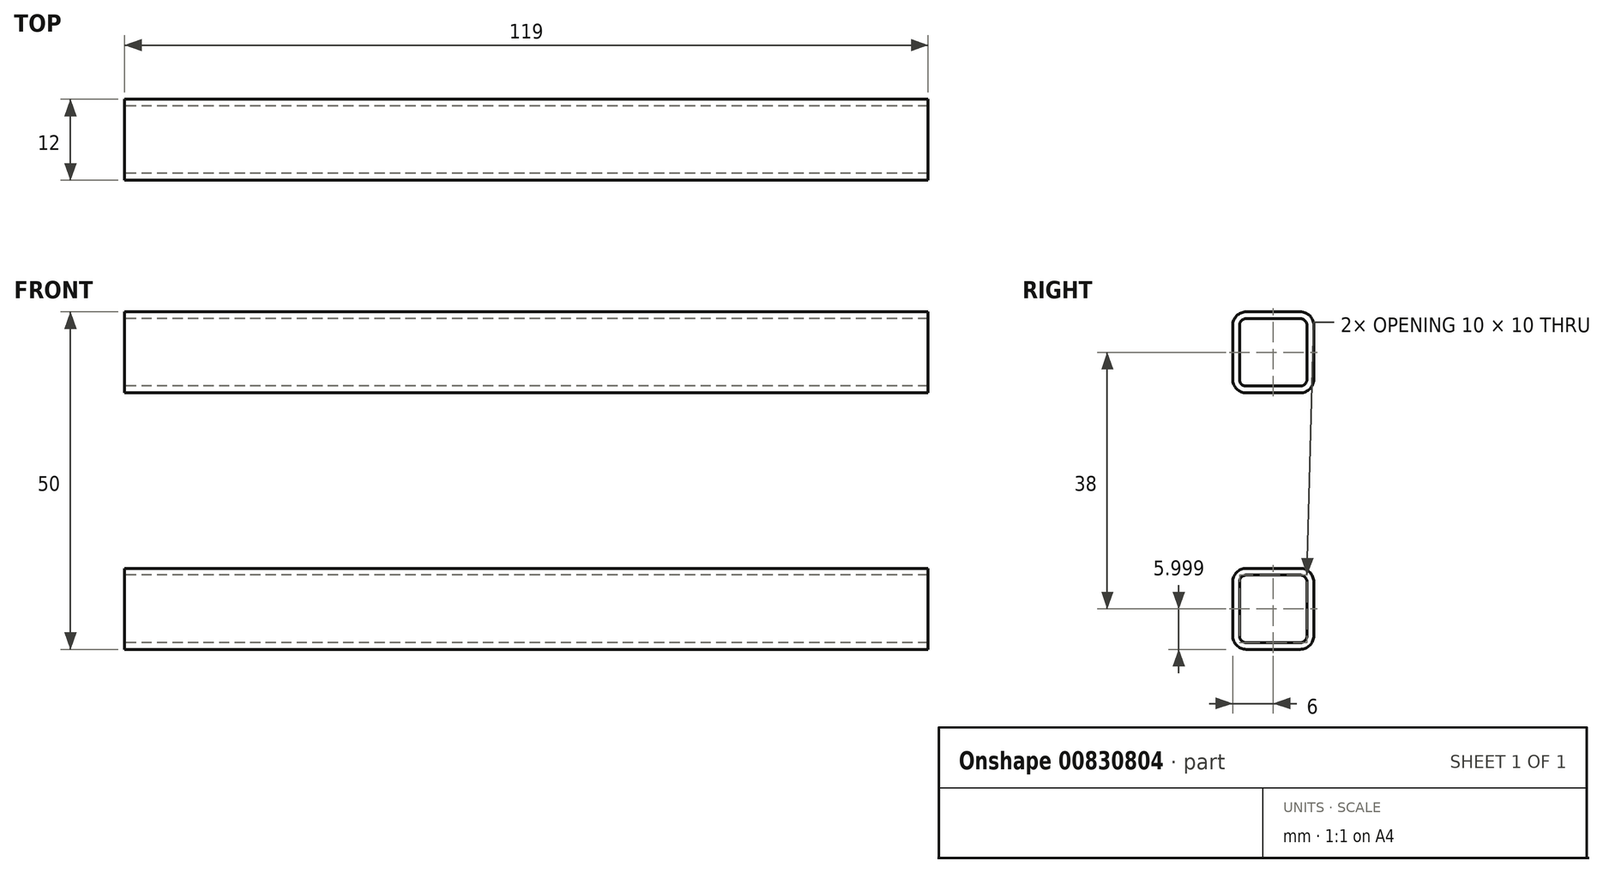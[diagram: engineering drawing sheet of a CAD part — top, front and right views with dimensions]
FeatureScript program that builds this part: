
annotation { "Feature Type Name" : "Feature", "Feature Type Description" : "" }
export const myFeature = defineFeature(function(context is Context, id is Id, definition is map)
    precondition{}
    {
        {
            var Q0;
            Q0=qCreatedBy(makeId("Front.planeOp"),FACE);
            var sketch = newSketch(context, id + "F0", { "sketchPlane" : qUnion([Q0])});
            skLineSegment(sketch, "E0", {"start": v(-60.2, 31.39) * mm, "end": v(58.8, 31.39) * mm});
            skLineSegment(sketch, "E1", {"start": v(-56.2, 36.39) * mm, "end": v(-56.2, -28.61) * mm});
            skLineSegment(sketch, "E2", {"start": v(53.8, 36.39) * mm, "end": v(53.8, -23.61) * mm});
            skLineSegment(sketch, "E3", {"start": v(58.8, -18.61) * mm, "end": v(-60.2, -18.61) * mm});
            skSolve(sketch);
        }
        {
            var Q0;
            Q0=sQuery(id+"F0.wireOp",VERTEX,"E1.end");
            var Q1;
            Q1=sQuery(id+"F0.wireOp",EDGE,"E1");
            cPlane(context, id + "F1", {"entities" : qUnion([Q0, Q1]), "cplaneType" : CPlaneType.LINE_POINT, "offset" : 150 * mm, "width" : 150 * mm, "height" : 150 * mm});
        }
        {
            var Q0;
            Q0=sQuery(id+"F0.wireOp",VERTEX,"E1.start");
            var Q1;
            Q1=sQuery(id+"F0.wireOp",EDGE,"E1");
            cPlane(context, id + "F2", {"entities" : qUnion([Q0, Q1]), "cplaneType" : CPlaneType.LINE_POINT, "offset" : 150 * mm, "width" : 150 * mm, "height" : 150 * mm});
        }
        {
            var Q0;
            Q0=qCreatedBy(id+"F1.planeOp",FACE);
            var sketch = newSketch(context, id + "F3", { "sketchPlane" : qUnion([Q0])});
            skLineSegment(sketch, "E4.bottom", {"start": v(-54.2, -12.5) * mm, "end": v(-46.2, -12.5) * mm});
            skLineSegment(sketch, "E4.top", {"start": v(-54.2, 12.5) * mm, "end": v(-46.2, 12.5) * mm});
            skLineSegment(sketch, "E4.left", {"start": v(-56.2, -10.5) * mm, "end": v(-56.2, 10.5) * mm});
            skLineSegment(sketch, "E4.right", {"start": v(-44.2, -10.5) * mm, "end": v(-44.2, 10.5) * mm});
            skPoint(sketch, "E5.visualSharp", {"position": v(-56.2, 12.5) * mm});
            skArc(sketch, "E5.filletArc", {"start": v(-54.2, 12.5) * mm, "mid": v(-55.62, 11.91) * mm, "end": v(-56.2, 10.5) * mm});
            skPoint(sketch, "E6.visualSharp", {"position": v(-44.2, 12.5) * mm});
            skArc(sketch, "E6.filletArc", {"start": v(-44.2, 10.5) * mm, "mid": v(-44.8, 11.91) * mm, "end": v(-46.2, 12.5) * mm});
            skPoint(sketch, "E7.visualSharp", {"position": v(-44.2, -12.5) * mm});
            skArc(sketch, "E7.filletArc", {"start": v(-46.2, -12.5) * mm, "mid": v(-44.8, -11.91) * mm, "end": v(-44.2, -10.5) * mm});
            skPoint(sketch, "E8.visualSharp", {"position": v(-56.2, -12.5) * mm});
            skArc(sketch, "E8.filletArc", {"start": v(-56.2, -10.5) * mm, "mid": v(-55.62, -11.91) * mm, "end": v(-54.2, -12.5) * mm});
            skArc(sketch, "E9.0", {"start": v(-54.2, 11.5) * mm, "mid": v(-54.91, 11.2) * mm, "end": v(-55.2, 10.5) * mm});
            skLineSegment(sketch, "E9.1", {"start": v(-55.2, -10.5) * mm, "end": v(-55.2, 10.5) * mm});
            skArc(sketch, "E9.2", {"start": v(-55.2, -10.5) * mm, "mid": v(-54.91, -11.2) * mm, "end": v(-54.2, -11.5) * mm});
            skLineSegment(sketch, "E9.3", {"start": v(-54.2, -11.5) * mm, "end": v(-46.2, -11.5) * mm});
            skArc(sketch, "E9.4", {"start": v(-46.2, -11.5) * mm, "mid": v(-45.5, -11.2) * mm, "end": v(-45.2, -10.5) * mm});
            skLineSegment(sketch, "E9.5", {"start": v(-54.2, 11.5) * mm, "end": v(-46.2, 11.5) * mm});
            skLineSegment(sketch, "E9.6", {"start": v(-45.2, -10.5) * mm, "end": v(-45.2, 10.5) * mm});
            skArc(sketch, "E9.7", {"start": v(-45.2, 10.5) * mm, "mid": v(-45.5, 11.2) * mm, "end": v(-46.2, 11.5) * mm});
            skSolve(sketch);
        }
        {
            var Q0;
            Q0=qSketchRegion(id+"F3",true);
            var Q1;
            Q1=qCreatedBy(id+"F2.planeOp",FACE);
            extrude(context, id + "F4", {"entities" : qUnion([Q0]), "endBound" : BoundingType.UP_TO_SURFACE, "oppositeDirection" : true, "endBoundEntityFace" : qUnion([Q1]), "offsetDistance" : 25 * mm, "depth" : 25 * mm});
        }
        {
            var Q0;
            Q0=sQuery(id+"F0.wireOp",EDGE,"E2");
            var Q1;
            Q1=sQuery(id+"F0.wireOp",VERTEX,"E2.end");
            cPlane(context, id + "F5", {"entities" : qUnion([Q0, Q1]), "cplaneType" : CPlaneType.LINE_POINT, "offset" : 150 * mm, "width" : 150 * mm, "height" : 150 * mm});
        }
        {
            var Q0;
            Q0=qCreatedBy(id+"F5.planeOp",FACE);
            var sketch = newSketch(context, id + "F6", { "sketchPlane" : qUnion([Q0])});
            skLineSegment(sketch, "E10.bottom", {"start": v(43.8, -12.5) * mm, "end": v(51.8, -12.5) * mm});
            skLineSegment(sketch, "E10.top", {"start": v(43.8, 12.5) * mm, "end": v(51.8, 12.5) * mm});
            skLineSegment(sketch, "E10.left", {"start": v(41.8, -10.5) * mm, "end": v(41.8, 10.5) * mm});
            skLineSegment(sketch, "E10.right", {"start": v(53.8, -10.5) * mm, "end": v(53.8, 10.5) * mm});
            skPoint(sketch, "E11.visualSharp", {"position": v(41.8, 12.5) * mm});
            skArc(sketch, "E11.filletArc", {"start": v(43.8, 12.5) * mm, "mid": v(42.38, 11.91) * mm, "end": v(41.8, 10.5) * mm});
            skPoint(sketch, "E12.visualSharp", {"position": v(53.8, 12.5) * mm});
            skArc(sketch, "E12.filletArc", {"start": v(53.8, 10.5) * mm, "mid": v(53.2, 11.91) * mm, "end": v(51.8, 12.5) * mm});
            skPoint(sketch, "E13.visualSharp", {"position": v(53.8, -12.5) * mm});
            skArc(sketch, "E13.filletArc", {"start": v(51.8, -12.5) * mm, "mid": v(53.2, -11.91) * mm, "end": v(53.8, -10.5) * mm});
            skPoint(sketch, "E14.visualSharp", {"position": v(41.8, -12.5) * mm});
            skArc(sketch, "E14.filletArc", {"start": v(41.8, -10.5) * mm, "mid": v(42.38, -11.91) * mm, "end": v(43.8, -12.5) * mm});
            skArc(sketch, "E15.0", {"start": v(43.8, 11.5) * mm, "mid": v(43.09, 11.2) * mm, "end": v(42.8, 10.5) * mm});
            skLineSegment(sketch, "E15.1", {"start": v(42.8, -10.5) * mm, "end": v(42.8, 10.5) * mm});
            skArc(sketch, "E15.2", {"start": v(42.8, -10.5) * mm, "mid": v(43.09, -11.2) * mm, "end": v(43.8, -11.5) * mm});
            skLineSegment(sketch, "E15.3", {"start": v(43.8, -11.5) * mm, "end": v(51.8, -11.5) * mm});
            skArc(sketch, "E15.4", {"start": v(51.8, -11.5) * mm, "mid": v(52.5, -11.2) * mm, "end": v(52.8, -10.5) * mm});
            skLineSegment(sketch, "E15.5", {"start": v(43.8, 11.5) * mm, "end": v(51.8, 11.5) * mm});
            skLineSegment(sketch, "E15.6", {"start": v(52.8, -10.5) * mm, "end": v(52.8, 10.5) * mm});
            skArc(sketch, "E15.7", {"start": v(52.8, 10.5) * mm, "mid": v(52.5, 11.2) * mm, "end": v(51.8, 11.5) * mm});
            skSolve(sketch);
        }
        {
            var Q0;
            Q0=qSketchRegion(id+"F6",true);
            var Q1;
            Q1=qCreatedBy(id+"F2.planeOp",FACE);
            extrude(context, id + "F7", {"entities" : qUnion([Q0]), "endBound" : BoundingType.UP_TO_SURFACE, "oppositeDirection" : true, "endBoundEntityFace" : qUnion([Q1]), "depth" : 25 * mm});
        }
        {
            var Q0;
            Q0=sQuery(id+"F0.wireOp",VERTEX,"E0.start");
            var Q1;
            Q1=sQuery(id+"F0.wireOp",EDGE,"E0");
            cPlane(context, id + "F8", {"entities" : qUnion([Q0, Q1]), "cplaneType" : CPlaneType.LINE_POINT, "offset" : 150 * mm, "width" : 150 * mm, "height" : 150 * mm});
        }
        {
            var Q0;
            Q0=qCreatedBy(id+"F8.planeOp",FACE);
            var sketch = newSketch(context, id + "F9", { "sketchPlane" : qUnion([Q0])});
            skLineSegment(sketch, "E16.bottom", {"start": v(4, 31.39) * mm, "end": v(-4, 31.39) * mm});
            skLineSegment(sketch, "E16.top", {"start": v(4, 19.39) * mm, "end": v(-4, 19.39) * mm});
            skLineSegment(sketch, "E16.left", {"start": v(6, 29.39) * mm, "end": v(6, 21.39) * mm});
            skLineSegment(sketch, "E16.right", {"start": v(-6, 29.39) * mm, "end": v(-6, 21.39) * mm});
            skPoint(sketch, "E17.visualSharp", {"position": v(6, 31.39) * mm});
            skArc(sketch, "E17.filletArc", {"start": v(6, 29.39) * mm, "mid": v(5.41, 30.8) * mm, "end": v(4, 31.39) * mm});
            skPoint(sketch, "E18.visualSharp", {"position": v(-6, 31.39) * mm});
            skArc(sketch, "E18.filletArc", {"start": v(-4, 31.39) * mm, "mid": v(-5.41, 30.8) * mm, "end": v(-6, 29.39) * mm});
            skPoint(sketch, "E19.visualSharp", {"position": v(-6, 19.39) * mm});
            skArc(sketch, "E19.filletArc", {"start": v(-6, 21.39) * mm, "mid": v(-5.41, 19.98) * mm, "end": v(-4, 19.39) * mm});
            skPoint(sketch, "E20.visualSharp", {"position": v(6, 19.39) * mm});
            skArc(sketch, "E20.filletArc", {"start": v(4, 19.39) * mm, "mid": v(5.41, 19.98) * mm, "end": v(6, 21.39) * mm});
            skArc(sketch, "E21.0", {"start": v(5, 29.39) * mm, "mid": v(4.7, 30.1) * mm, "end": v(4, 30.39) * mm});
            skLineSegment(sketch, "E21.1", {"start": v(5, 29.39) * mm, "end": v(5, 21.39) * mm});
            skArc(sketch, "E21.2", {"start": v(4, 20.39) * mm, "mid": v(4.7, 20.68) * mm, "end": v(5, 21.39) * mm});
            skLineSegment(sketch, "E21.3", {"start": v(4, 20.39) * mm, "end": v(-4, 20.39) * mm});
            skArc(sketch, "E21.4", {"start": v(-5, 21.39) * mm, "mid": v(-4.7, 20.68) * mm, "end": v(-4, 20.39) * mm});
            skLineSegment(sketch, "E21.5", {"start": v(4, 30.39) * mm, "end": v(-4, 30.39) * mm});
            skLineSegment(sketch, "E21.6", {"start": v(-5, 29.39) * mm, "end": v(-5, 21.39) * mm});
            skArc(sketch, "E21.7", {"start": v(-4, 30.39) * mm, "mid": v(-4.7, 30.1) * mm, "end": v(-5, 29.39) * mm});
            skPoint(sketch, "E22", {"position": v(0, 19.39) * mm});
            skSolve(sketch);
        }
        {
            var Q0;
            Q0=sQuery(id+"F0.wireOp",VERTEX,"E0.end");
            var Q1;
            Q1=sQuery(id+"F0.wireOp",EDGE,"E0");
            cPlane(context, id + "F10", {"entities" : qUnion([Q0, Q1]), "cplaneType" : CPlaneType.LINE_POINT, "offset" : 150 * mm, "width" : 150 * mm, "height" : 150 * mm});
        }
        {
            var Q0;
            Q0=qSketchRegion(id+"F9",true);
            var Q1;
            Q1=qCreatedBy(id+"F10.planeOp",FACE);
            extrude(context, id + "F11", {"entities" : qUnion([Q0]), "endBound" : BoundingType.UP_TO_SURFACE, "endBoundEntityFace" : qUnion([Q1]), "depth" : 25 * mm});
        }
        {
            var Q0;
            Q0=makeQuery(id+"F11.opExtrude","SWEPT_BODY",BODY,{"disambiguationData":[OSD([sQuery(id+"F9.wireOp",EDGE,"E16.bottom"),sQuery(id+"F9.wireOp",EDGE,"E16.top"),sQuery(id+"F9.wireOp",EDGE,"E16.left"),sQuery(id+"F9.wireOp",EDGE,"E16.right"),sQuery(id+"F9.wireOp",EDGE,"E17.filletArc"),sQuery(id+"F9.wireOp",EDGE,"E18.filletArc"),sQuery(id+"F9.wireOp",EDGE,"E19.filletArc"),sQuery(id+"F9.wireOp",EDGE,"E20.filletArc"),sQuery(id+"F9.wireOp",EDGE,"E21.0"),sQuery(id+"F9.wireOp",EDGE,"E21.1"),sQuery(id+"F9.wireOp",EDGE,"E21.2"),sQuery(id+"F9.wireOp",EDGE,"E21.3"),sQuery(id+"F9.wireOp",EDGE,"E21.4"),sQuery(id+"F9.wireOp",EDGE,"E21.5"),sQuery(id+"F9.wireOp",EDGE,"E21.6"),sQuery(id+"F9.wireOp",EDGE,"E21.7")])]});
            var Q1;
            Q1=sQuery(id+"F9.wireOp",VERTEX,"E22");
            var Q2;
            Q2=sQuery(id+"F0.wireOp",VERTEX,"E3.end");
            transform(context, id + "F12", {"entities" : qUnion([Q0]), "transformType" : TransformType.TRANSLATION_ENTITY, "oppositeDirectionEntity" : false, "transformLine" : qUnion([Q1, Q2]), "makeCopy" : true});
        }
        {
            var Q0;
            Q0=makeQuery(id+"F11.opExtrude","SWEPT_BODY",BODY,{"disambiguationData":[OSD([sQuery(id+"F9.wireOp",EDGE,"E16.bottom"),sQuery(id+"F9.wireOp",EDGE,"E16.top"),sQuery(id+"F9.wireOp",EDGE,"E16.left"),sQuery(id+"F9.wireOp",EDGE,"E16.right"),sQuery(id+"F9.wireOp",EDGE,"E17.filletArc"),sQuery(id+"F9.wireOp",EDGE,"E18.filletArc"),sQuery(id+"F9.wireOp",EDGE,"E19.filletArc"),sQuery(id+"F9.wireOp",EDGE,"E20.filletArc"),sQuery(id+"F9.wireOp",EDGE,"E21.0"),sQuery(id+"F9.wireOp",EDGE,"E21.1"),sQuery(id+"F9.wireOp",EDGE,"E21.2"),sQuery(id+"F9.wireOp",EDGE,"E21.3"),sQuery(id+"F9.wireOp",EDGE,"E21.4"),sQuery(id+"F9.wireOp",EDGE,"E21.5"),sQuery(id+"F9.wireOp",EDGE,"E21.6"),sQuery(id+"F9.wireOp",EDGE,"E21.7")])]});
            var Q1;
            Q1=makeQuery(id+"F12.opPattern","COPY",BODY,{"derivedFrom":makeQuery(id+"F11.opExtrude","SWEPT_BODY",BODY,{"disambiguationData":[OSD([sQuery(id+"F9.wireOp",EDGE,"E16.bottom"),sQuery(id+"F9.wireOp",EDGE,"E16.top"),sQuery(id+"F9.wireOp",EDGE,"E16.left"),sQuery(id+"F9.wireOp",EDGE,"E16.right"),sQuery(id+"F9.wireOp",EDGE,"E17.filletArc"),sQuery(id+"F9.wireOp",EDGE,"E18.filletArc"),sQuery(id+"F9.wireOp",EDGE,"E19.filletArc"),sQuery(id+"F9.wireOp",EDGE,"E20.filletArc"),sQuery(id+"F9.wireOp",EDGE,"E21.0"),sQuery(id+"F9.wireOp",EDGE,"E21.1"),sQuery(id+"F9.wireOp",EDGE,"E21.2"),sQuery(id+"F9.wireOp",EDGE,"E21.3"),sQuery(id+"F9.wireOp",EDGE,"E21.4"),sQuery(id+"F9.wireOp",EDGE,"E21.5"),sQuery(id+"F9.wireOp",EDGE,"E21.6"),sQuery(id+"F9.wireOp",EDGE,"E21.7")])]}),"instanceName":"1"});
            var Q2;
            Q2=makeQuery(id+"F4.opExtrude","SWEPT_BODY",BODY,{"disambiguationData":[OSD([sQuery(id+"F3.wireOp",EDGE,"E4.bottom"),sQuery(id+"F3.wireOp",EDGE,"E4.top"),sQuery(id+"F3.wireOp",EDGE,"E4.left"),sQuery(id+"F3.wireOp",EDGE,"E4.right"),sQuery(id+"F3.wireOp",EDGE,"E5.filletArc"),sQuery(id+"F3.wireOp",EDGE,"E6.filletArc"),sQuery(id+"F3.wireOp",EDGE,"E7.filletArc"),sQuery(id+"F3.wireOp",EDGE,"E8.filletArc"),sQuery(id+"F3.wireOp",EDGE,"E9.0"),sQuery(id+"F3.wireOp",EDGE,"E9.1"),sQuery(id+"F3.wireOp",EDGE,"E9.2"),sQuery(id+"F3.wireOp",EDGE,"E9.3"),sQuery(id+"F3.wireOp",EDGE,"E9.4"),sQuery(id+"F3.wireOp",EDGE,"E9.5"),sQuery(id+"F3.wireOp",EDGE,"E9.6"),sQuery(id+"F3.wireOp",EDGE,"E9.7")])]});
            var Q3;
            Q3=makeQuery(id+"F7.opExtrude","SWEPT_BODY",BODY,{"disambiguationData":[OSD([sQuery(id+"F6.wireOp",EDGE,"E10.bottom"),sQuery(id+"F6.wireOp",EDGE,"E10.top"),sQuery(id+"F6.wireOp",EDGE,"E10.left"),sQuery(id+"F6.wireOp",EDGE,"E10.right"),sQuery(id+"F6.wireOp",EDGE,"E11.filletArc"),sQuery(id+"F6.wireOp",EDGE,"E12.filletArc"),sQuery(id+"F6.wireOp",EDGE,"E13.filletArc"),sQuery(id+"F6.wireOp",EDGE,"E14.filletArc"),sQuery(id+"F6.wireOp",EDGE,"E15.0"),sQuery(id+"F6.wireOp",EDGE,"E15.1"),sQuery(id+"F6.wireOp",EDGE,"E15.2"),sQuery(id+"F6.wireOp",EDGE,"E15.3"),sQuery(id+"F6.wireOp",EDGE,"E15.4"),sQuery(id+"F6.wireOp",EDGE,"E15.5"),sQuery(id+"F6.wireOp",EDGE,"E15.6"),sQuery(id+"F6.wireOp",EDGE,"E15.7")])]});
            booleanBodies(context, id + "F13", {"operationType" : BooleanOperationType.SUBTRACTION, "tools" : qUnion([Q0, Q1]), "targets" : qUnion([Q2, Q3]), "offset" : true, "offsetAll" : true, "offsetDistance" : 1 * mm, "keepTools" : true});
        }
        {
            var Q0;
            Q0=makeQuery(id+"F13.tempBoolean.opBoolean","SPLIT",BODY,{"disambiguationData":[OD(2.0)],"derivedFrom":makeQuery(id+"F7.opExtrude","SWEPT_BODY",BODY,{"disambiguationData":[OSD([sQuery(id+"F6.wireOp",EDGE,"E10.bottom"),sQuery(id+"F6.wireOp",EDGE,"E10.top"),sQuery(id+"F6.wireOp",EDGE,"E10.left"),sQuery(id+"F6.wireOp",EDGE,"E10.right"),sQuery(id+"F6.wireOp",EDGE,"E11.filletArc"),sQuery(id+"F6.wireOp",EDGE,"E12.filletArc"),sQuery(id+"F6.wireOp",EDGE,"E13.filletArc"),sQuery(id+"F6.wireOp",EDGE,"E14.filletArc"),sQuery(id+"F6.wireOp",EDGE,"E15.0"),sQuery(id+"F6.wireOp",EDGE,"E15.1"),sQuery(id+"F6.wireOp",EDGE,"E15.2"),sQuery(id+"F6.wireOp",EDGE,"E15.3"),sQuery(id+"F6.wireOp",EDGE,"E15.4"),sQuery(id+"F6.wireOp",EDGE,"E15.5"),sQuery(id+"F6.wireOp",EDGE,"E15.6"),sQuery(id+"F6.wireOp",EDGE,"E15.7")])]})});
            var Q1;
            Q1=makeQuery(id+"F13.tempBoolean.opBoolean","SPLIT",BODY,{"disambiguationData":[OD(1.0)],"derivedFrom":makeQuery(id+"F7.opExtrude","SWEPT_BODY",BODY,{"disambiguationData":[OSD([sQuery(id+"F6.wireOp",EDGE,"E10.bottom"),sQuery(id+"F6.wireOp",EDGE,"E10.top"),sQuery(id+"F6.wireOp",EDGE,"E10.left"),sQuery(id+"F6.wireOp",EDGE,"E10.right"),sQuery(id+"F6.wireOp",EDGE,"E11.filletArc"),sQuery(id+"F6.wireOp",EDGE,"E12.filletArc"),sQuery(id+"F6.wireOp",EDGE,"E13.filletArc"),sQuery(id+"F6.wireOp",EDGE,"E14.filletArc"),sQuery(id+"F6.wireOp",EDGE,"E15.0"),sQuery(id+"F6.wireOp",EDGE,"E15.1"),sQuery(id+"F6.wireOp",EDGE,"E15.2"),sQuery(id+"F6.wireOp",EDGE,"E15.3"),sQuery(id+"F6.wireOp",EDGE,"E15.4"),sQuery(id+"F6.wireOp",EDGE,"E15.5"),sQuery(id+"F6.wireOp",EDGE,"E15.6"),sQuery(id+"F6.wireOp",EDGE,"E15.7")])]})});
            var Q2;
            Q2=makeQuery(id+"F13.tempBoolean.opBoolean","SPLIT",BODY,{"disambiguationData":[OD(4.0)],"derivedFrom":makeQuery(id+"F7.opExtrude","SWEPT_BODY",BODY,{"disambiguationData":[OSD([sQuery(id+"F6.wireOp",EDGE,"E10.bottom"),sQuery(id+"F6.wireOp",EDGE,"E10.top"),sQuery(id+"F6.wireOp",EDGE,"E10.left"),sQuery(id+"F6.wireOp",EDGE,"E10.right"),sQuery(id+"F6.wireOp",EDGE,"E11.filletArc"),sQuery(id+"F6.wireOp",EDGE,"E12.filletArc"),sQuery(id+"F6.wireOp",EDGE,"E13.filletArc"),sQuery(id+"F6.wireOp",EDGE,"E14.filletArc"),sQuery(id+"F6.wireOp",EDGE,"E15.0"),sQuery(id+"F6.wireOp",EDGE,"E15.1"),sQuery(id+"F6.wireOp",EDGE,"E15.2"),sQuery(id+"F6.wireOp",EDGE,"E15.3"),sQuery(id+"F6.wireOp",EDGE,"E15.4"),sQuery(id+"F6.wireOp",EDGE,"E15.5"),sQuery(id+"F6.wireOp",EDGE,"E15.6"),sQuery(id+"F6.wireOp",EDGE,"E15.7")])]})});
            var Q3;
            Q3=makeQuery(id+"F13.tempBoolean.opBoolean","SPLIT",BODY,{"disambiguationData":[OD(3.0)],"derivedFrom":makeQuery(id+"F7.opExtrude","SWEPT_BODY",BODY,{"disambiguationData":[OSD([sQuery(id+"F6.wireOp",EDGE,"E10.bottom"),sQuery(id+"F6.wireOp",EDGE,"E10.top"),sQuery(id+"F6.wireOp",EDGE,"E10.left"),sQuery(id+"F6.wireOp",EDGE,"E10.right"),sQuery(id+"F6.wireOp",EDGE,"E11.filletArc"),sQuery(id+"F6.wireOp",EDGE,"E12.filletArc"),sQuery(id+"F6.wireOp",EDGE,"E13.filletArc"),sQuery(id+"F6.wireOp",EDGE,"E14.filletArc"),sQuery(id+"F6.wireOp",EDGE,"E15.0"),sQuery(id+"F6.wireOp",EDGE,"E15.1"),sQuery(id+"F6.wireOp",EDGE,"E15.2"),sQuery(id+"F6.wireOp",EDGE,"E15.3"),sQuery(id+"F6.wireOp",EDGE,"E15.4"),sQuery(id+"F6.wireOp",EDGE,"E15.5"),sQuery(id+"F6.wireOp",EDGE,"E15.6"),sQuery(id+"F6.wireOp",EDGE,"E15.7")])]})});
            var Q4;
            Q4=makeQuery(id+"F13.tempBoolean.opBoolean","SPLIT",BODY,{"disambiguationData":[OD(1.0)],"derivedFrom":makeQuery(id+"F4.opExtrude","SWEPT_BODY",BODY,{"disambiguationData":[OSD([sQuery(id+"F3.wireOp",EDGE,"E4.bottom"),sQuery(id+"F3.wireOp",EDGE,"E4.top"),sQuery(id+"F3.wireOp",EDGE,"E4.left"),sQuery(id+"F3.wireOp",EDGE,"E4.right"),sQuery(id+"F3.wireOp",EDGE,"E5.filletArc"),sQuery(id+"F3.wireOp",EDGE,"E6.filletArc"),sQuery(id+"F3.wireOp",EDGE,"E7.filletArc"),sQuery(id+"F3.wireOp",EDGE,"E8.filletArc"),sQuery(id+"F3.wireOp",EDGE,"E9.0"),sQuery(id+"F3.wireOp",EDGE,"E9.1"),sQuery(id+"F3.wireOp",EDGE,"E9.2"),sQuery(id+"F3.wireOp",EDGE,"E9.3"),sQuery(id+"F3.wireOp",EDGE,"E9.4"),sQuery(id+"F3.wireOp",EDGE,"E9.5"),sQuery(id+"F3.wireOp",EDGE,"E9.6"),sQuery(id+"F3.wireOp",EDGE,"E9.7")])]})});
            var Q5;
            Q5=makeQuery(id+"F13.tempBoolean.opBoolean","SPLIT",BODY,{"disambiguationData":[OD(2.0)],"derivedFrom":makeQuery(id+"F4.opExtrude","SWEPT_BODY",BODY,{"disambiguationData":[OSD([sQuery(id+"F3.wireOp",EDGE,"E4.bottom"),sQuery(id+"F3.wireOp",EDGE,"E4.top"),sQuery(id+"F3.wireOp",EDGE,"E4.left"),sQuery(id+"F3.wireOp",EDGE,"E4.right"),sQuery(id+"F3.wireOp",EDGE,"E5.filletArc"),sQuery(id+"F3.wireOp",EDGE,"E6.filletArc"),sQuery(id+"F3.wireOp",EDGE,"E7.filletArc"),sQuery(id+"F3.wireOp",EDGE,"E8.filletArc"),sQuery(id+"F3.wireOp",EDGE,"E9.0"),sQuery(id+"F3.wireOp",EDGE,"E9.1"),sQuery(id+"F3.wireOp",EDGE,"E9.2"),sQuery(id+"F3.wireOp",EDGE,"E9.3"),sQuery(id+"F3.wireOp",EDGE,"E9.4"),sQuery(id+"F3.wireOp",EDGE,"E9.5"),sQuery(id+"F3.wireOp",EDGE,"E9.6"),sQuery(id+"F3.wireOp",EDGE,"E9.7")])]})});
            var Q6;
            Q6=makeQuery(id+"F13.tempBoolean.opBoolean","SPLIT",BODY,{"disambiguationData":[OD(4.0)],"derivedFrom":makeQuery(id+"F4.opExtrude","SWEPT_BODY",BODY,{"disambiguationData":[OSD([sQuery(id+"F3.wireOp",EDGE,"E4.bottom"),sQuery(id+"F3.wireOp",EDGE,"E4.top"),sQuery(id+"F3.wireOp",EDGE,"E4.left"),sQuery(id+"F3.wireOp",EDGE,"E4.right"),sQuery(id+"F3.wireOp",EDGE,"E5.filletArc"),sQuery(id+"F3.wireOp",EDGE,"E6.filletArc"),sQuery(id+"F3.wireOp",EDGE,"E7.filletArc"),sQuery(id+"F3.wireOp",EDGE,"E8.filletArc"),sQuery(id+"F3.wireOp",EDGE,"E9.0"),sQuery(id+"F3.wireOp",EDGE,"E9.1"),sQuery(id+"F3.wireOp",EDGE,"E9.2"),sQuery(id+"F3.wireOp",EDGE,"E9.3"),sQuery(id+"F3.wireOp",EDGE,"E9.4"),sQuery(id+"F3.wireOp",EDGE,"E9.5"),sQuery(id+"F3.wireOp",EDGE,"E9.6"),sQuery(id+"F3.wireOp",EDGE,"E9.7")])]})});
            var Q7;
            Q7=makeQuery(id+"F13.tempBoolean.opBoolean","SPLIT",BODY,{"disambiguationData":[OD(3.0)],"derivedFrom":makeQuery(id+"F4.opExtrude","SWEPT_BODY",BODY,{"disambiguationData":[OSD([sQuery(id+"F3.wireOp",EDGE,"E4.bottom"),sQuery(id+"F3.wireOp",EDGE,"E4.top"),sQuery(id+"F3.wireOp",EDGE,"E4.left"),sQuery(id+"F3.wireOp",EDGE,"E4.right"),sQuery(id+"F3.wireOp",EDGE,"E5.filletArc"),sQuery(id+"F3.wireOp",EDGE,"E6.filletArc"),sQuery(id+"F3.wireOp",EDGE,"E7.filletArc"),sQuery(id+"F3.wireOp",EDGE,"E8.filletArc"),sQuery(id+"F3.wireOp",EDGE,"E9.0"),sQuery(id+"F3.wireOp",EDGE,"E9.1"),sQuery(id+"F3.wireOp",EDGE,"E9.2"),sQuery(id+"F3.wireOp",EDGE,"E9.3"),sQuery(id+"F3.wireOp",EDGE,"E9.4"),sQuery(id+"F3.wireOp",EDGE,"E9.5"),sQuery(id+"F3.wireOp",EDGE,"E9.6"),sQuery(id+"F3.wireOp",EDGE,"E9.7")])]})});
            deleteBodies(context, id + "F14", {"entities" : qUnion([Q0, Q1, Q2, Q3, Q4, Q5, Q6, Q7])});
        }
        {
            var Q0;
            {var subQ0=sQuery(id+"F3.wireOp",EDGE,"E4.left");var subQ10=sQuery(id+"F3.wireOp",EDGE,"E5.filletArc");Q0=makeQuery(id+"F13.tempBoolean.opBoolean","SPLIT",FACE,{"disambiguationData":[TD([makeQuery(id+"F4.opExtrude","SWEPT_FACE",FACE,{"disambiguationData":[OSD([subQ10])]})])],"derivedFrom":makeQuery(id+"F4.opExtrude","SWEPT_FACE",FACE,{"disambiguationData":[OSD([subQ0])]})});}
            var sketch = newSketch(context, id + "F15", { "sketchPlane" : qUnion([Q0])});
            skLineSegment(sketch, "E23", {"start": v(0, -5.61) * mm, "end": v(0, -19.61) * mm, "construction": true});
            skPoint(sketch, "E24", {"position": v(0, -12.61) * mm});
            skSolve(sketch);
        }
    });
